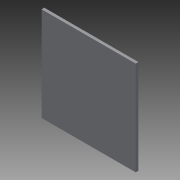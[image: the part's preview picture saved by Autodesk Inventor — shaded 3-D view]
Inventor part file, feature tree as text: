
AUTODESK INVENTOR PART (.ipt)
format: ipt  version: 2013 (Build 170138000, 138)  size: 160,768 bytes
history: native  units: mm
features: extrude x2, sketch x2, other x1
ambient origin geometry x8: Origin, YZ Plane, XZ Plane, XY Plane, X Axis, Y Axis, Z Axis, Center Point
feature tree (5):
  other  "ソリッド1"
  extrude  "押し出し1"  Depth=104.0mm
  extrude  "押し出し2"  Depth=104.0mm
  sketch  "スケッチ1"
  sketch  "スケッチ2"
